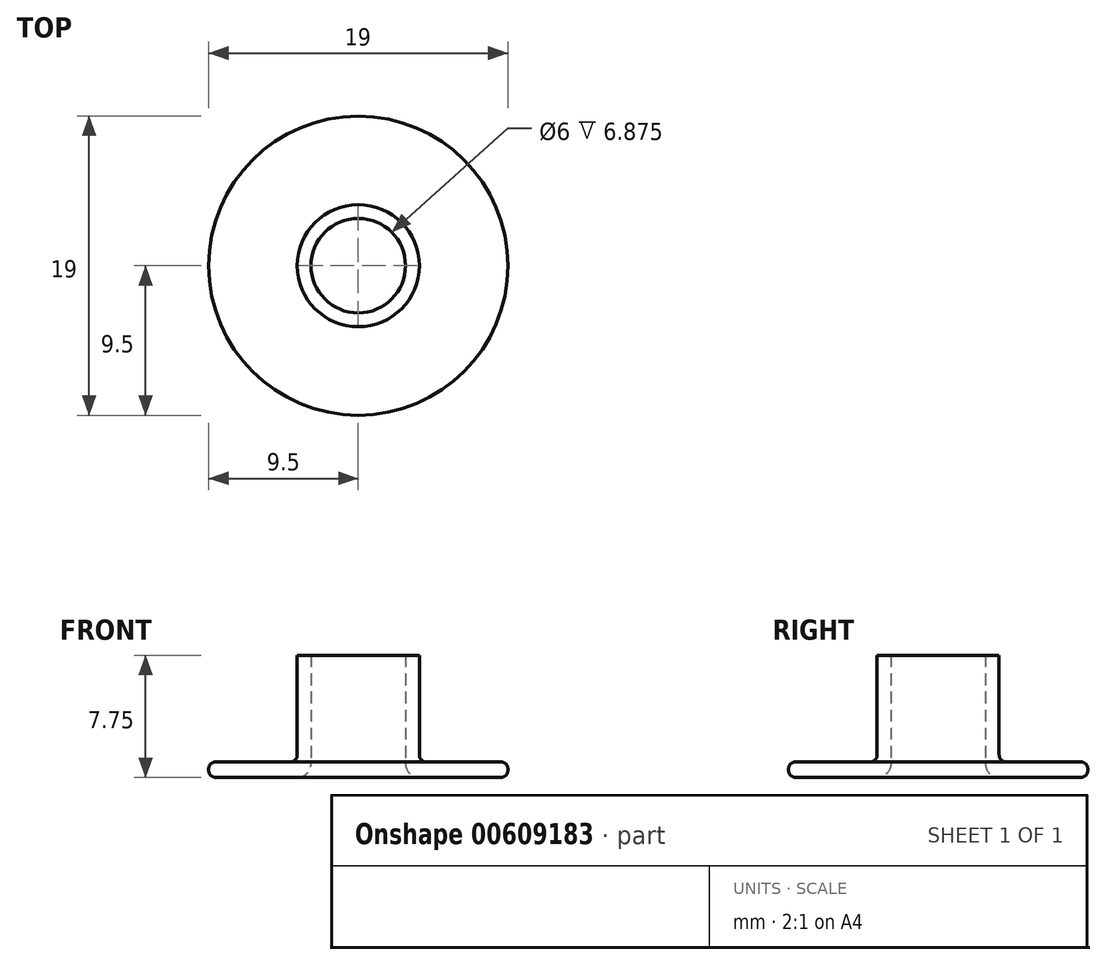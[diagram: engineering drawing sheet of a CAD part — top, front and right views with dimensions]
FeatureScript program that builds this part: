
annotation { "Feature Type Name" : "Feature", "Feature Type Description" : "" }
export const myFeature = defineFeature(function(context is Context, id is Id, definition is map)
    precondition{}
    {
        {
            var Q0;
            Q0=qCreatedBy(makeId("Front.planeOp"),FACE);
            var sketch = newSketch(context, id + "F0", { "sketchPlane" : qUnion([Q0])});
            skLineSegment(sketch, "E0", {"start": v(-3.88, 0) * mm, "end": v(-9.06, 0) * mm});
            skLineSegment(sketch, "E1", {"start": v(-9.5, 0.44) * mm, "end": v(-9.5, 0.54) * mm});
            skLineSegment(sketch, "E2", {"start": v(-9.06, 0.98) * mm, "end": v(-4.31, 0.98) * mm});
            skLineSegment(sketch, "E3", {"start": v(-3.88, 1.42) * mm, "end": v(-3.88, 7.75) * mm});
            skLineSegment(sketch, "E4", {"start": v(-3.88, 7.75) * mm, "end": v(-3, 7.75) * mm});
            skLineSegment(sketch, "E5", {"start": v(-3, 7.75) * mm, "end": v(-3, 0.87) * mm});
            skLineSegment(sketch, "E6", {"start": v(-3, 0) * mm, "end": v(0, 0) * mm, "construction": true});
            skPoint(sketch, "E7.visualSharp", {"position": v(-9.5, 0.98) * mm});
            skArc(sketch, "E7.filletArc", {"start": v(-9.06, 0.98) * mm, "mid": v(-9.37, 0.85) * mm, "end": v(-9.5, 0.54) * mm});
            skPoint(sketch, "E8.visualSharp", {"position": v(-9.5, 0) * mm});
            skArc(sketch, "E8.filletArc", {"start": v(-9.5, 0.44) * mm, "mid": v(-9.37, 0.13) * mm, "end": v(-9.06, 0) * mm});
            skPoint(sketch, "E9.visualSharp", {"position": v(-3.88, 0.98) * mm});
            skArc(sketch, "E9.filletArc", {"start": v(-4.31, 0.98) * mm, "mid": v(-4, 1.1) * mm, "end": v(-3.88, 1.42) * mm});
            skPoint(sketch, "E10.visualSharp", {"position": v(-3, 0) * mm});
            skArc(sketch, "E10.filletArc", {"start": v(-3.88, 0) * mm, "mid": v(-3.26, 0.26) * mm, "end": v(-3, 0.87) * mm});
            skLineSegment(sketch, "E11", {"start": v(0, 0) * mm, "end": v(0, 7.75) * mm, "construction": true});
            skSolve(sketch);
        }
        {
            var Q0;
            Q0 = qSketchRegion(id + "F0", true);
            var Q1;
            Q1=sQuery(id+"F0.wireOp",EDGE,"E11");
            revolve(context, id + "F1", {"entities" : qUnion([Q0]), "axis" : qUnion([Q1]), "revolveType" : RevolveType.FULL});
        }
    });
